FCSTD DOCUMENT  (FreeCAD 0.19R24276 (Git))
Label: Master_sketch
License: All rights reserved
LicenseURL: http://en.wikipedia.org/wiki/All_rights_reserved
objects: Sketcher::SketchObject×1, PartDesign::Body×1
note: 2 computed .brp shape members not serialized (recipe doc carries the construction recipe); baked Part::Feature solids carry a one-line shape summary decoded from their .brp

FEATURE [Sketcher::SketchObject] Sketch
  FullyConstrained = false
  MapMode = 5
  Support = -> [XY_Plane]
  sketch-geometry (44):
    g0: Circle CenterX=0 CenterY=-54 CenterZ=0 NormalX=0 NormalY=0 NormalZ=1 AngleXU=0 Radius=4
    g1: LineSegment StartX=-57.9645 StartY=-38.8963 StartZ=0 EndX=-1.26483 EndY=-57.7948 EndZ=0
    g2: LineSegment StartX=-45 StartY=0 StartZ=0 EndX=-57.9645 EndY=-38.8963 EndZ=0
    g3: LineSegment StartX=0 StartY=-54 StartZ=0 EndX=-1.26483 EndY=-57.7948 EndZ=0
    g4: LineSegment StartX=1.39757 StartY=-57.7479 StartZ=0 EndX=58.5823 EndY=-36.4241 EndZ=0
    g5: LineSegment StartX=45 StartY=0 StartZ=0 EndX=58.5823 EndY=-36.4241 EndZ=0
    g6: LineSegment StartX=0 StartY=-54 StartZ=0 EndX=1.39757 EndY=-57.7479 EndZ=0
    g7: LineSegment StartX=-45 StartY=0 StartZ=0 EndX=45 EndY=0 EndZ=0
    g8: LineSegment StartX=0 StartY=0 StartZ=0 EndX=0 EndY=-54 EndZ=0
    g9: Circle CenterX=0 CenterY=0 CenterZ=0 NormalX=0 NormalY=0 NormalZ=1 AngleXU=0 Radius=90
    g10: LineSegment StartX=-45 StartY=0 StartZ=0 EndX=-31.8819 EndY=-39.2255 EndZ=0
    g11: Circle CenterX=0 CenterY=54 CenterZ=0 NormalX=0 NormalY=0 NormalZ=1 AngleXU=0 Radius=4
    g12: LineSegment StartX=0 StartY=0 StartZ=0 EndX=0 EndY=54 EndZ=0
    g13: Circle CenterX=0 CenterY=220 CenterZ=0 NormalX=0 NormalY=0 NormalZ=1 AngleXU=0 Radius=20
    g14: LineSegment StartX=45 StartY=0 StartZ=0 EndX=56.689 EndY=42.3716 EndZ=0
    g15: LineSegment StartX=-29.7255 StartY=-48.3086 StartZ=0 EndX=-26.8797 EndY=-39.7704 EndZ=0
    g16: LineSegment StartX=-29.7255 StartY=-48.3086 StartZ=0 EndX=-32.5714 EndY=-56.8468 EndZ=0
    g17: Circle CenterX=-45 CenterY=0 CenterZ=0 NormalX=0 NormalY=0 NormalZ=1 AngleXU=0 Radius=41
    g18: Circle CenterX=45 CenterY=0 CenterZ=0 NormalX=0 NormalY=0 NormalZ=1 AngleXU=0 Radius=41
    g19: LineSegment StartX=-119.998 StartY=-134.375 StartZ=0 EndX=119.998 EndY=-135.625 EndZ=0
    g20: LineSegment StartX=0 StartY=0 StartZ=0 EndX=0 EndY=-135 EndZ=0
    g21: LineSegment StartX=-119.998 StartY=-134.375 StartZ=0 EndX=-94.9987 EndY=-134.505 EndZ=0
    g22: LineSegment StartX=-94.9987 StartY=-134.505 StartZ=0 EndX=-94.8737 EndY=-110.506 EndZ=0
    g23: LineSegment StartX=-94.8737 StartY=-110.506 StartZ=0 EndX=-119.873 EndY=-110.375 EndZ=0
    g24: LineSegment StartX=-119.873 StartY=-110.375 StartZ=0 EndX=-119.998 EndY=-134.375 EndZ=0
    g25: LineSegment StartX=119.998 StartY=-135.625 StartZ=0 EndX=94.9987 EndY=-135.495 EndZ=0
    g26: LineSegment StartX=94.9987 StartY=-135.495 StartZ=0 EndX=95.1237 EndY=-111.495 EndZ=0
    g27: LineSegment StartX=95.1237 StartY=-111.495 StartZ=0 EndX=120.123 EndY=-111.625 EndZ=0
    g28: LineSegment StartX=120.123 StartY=-111.625 StartZ=0 EndX=119.998 EndY=-135.625 EndZ=0
    g29: LineSegment StartX=0 StartY=-135 StartZ=0 EndX=-86.2867 EndY=-103.084 EndZ=0
    g30: LineSegment StartX=0 StartY=-135 StartZ=0 EndX=86.6144 EndY=-103.985 EndZ=0
    g31: LineSegment StartX=86.6144 StartY=-103.985 StartZ=0 EndX=97.6158 EndY=-134.708 EndZ=0
    g32: LineSegment StartX=97.6158 StartY=-134.708 StartZ=0 EndX=128.339 EndY=-123.706 EndZ=0
    g33: LineSegment StartX=128.339 StartY=-123.706 StartZ=0 EndX=117.337 EndY=-92.9833 EndZ=0
    g34: LineSegment StartX=-86.2867 StartY=-103.084 StartZ=0 EndX=-110.929 EndY=-107.297 EndZ=0
    g35: LineSegment StartX=-110.929 StartY=-107.297 StartZ=0 EndX=-115.142 EndY=-82.6549 EndZ=0
    g36: LineSegment StartX=-115.142 StartY=-82.6549 StartZ=0 EndX=-90.4997 EndY=-78.442 EndZ=0
    g37: LineSegment StartX=-90.4997 StartY=-78.442 StartZ=0 EndX=-86.2867 EndY=-103.084 EndZ=0
    g38: LineSegment StartX=-100.714 StartY=-92.8697 StartZ=0 EndX=-90.4997 EndY=-78.442 EndZ=0
    g39: LineSegment StartX=-115.142 StartY=-82.6549 StartZ=0 EndX=-86.2867 EndY=-103.084 EndZ=0
    g40: LineSegment StartX=-31.8812 StartY=-137.215 StartZ=0 EndX=34.0407 EndY=-137.215 EndZ=0
    g41: LineSegment StartX=34.0407 StartY=-137.215 StartZ=0 EndX=34.0407 EndY=-145.036 EndZ=0
    g42: LineSegment StartX=34.0407 StartY=-145.036 StartZ=0 EndX=-31.8812 EndY=-145.036 EndZ=0
    g43: LineSegment StartX=-31.8812 StartY=-145.036 StartZ=0 EndX=-31.8812 EndY=-137.215 EndZ=0
  constraints (109):
    c: Diameter(g0) = 8
    c: PointOnObject(g1,g0)
    c: Perpendicular(g1,g2)
    c: Coincident(g3,g0)
    c: Coincident(g3,g1)
    c: Perpendicular(g3,g1)
    c: PointOnObject(g4,g0)
    c: Coincident(g5,g4)
    c: Perpendicular(g5,g4)
    c: Coincident(g6,g0)
    c: Coincident(g6,g4)
    c: Perpendicular(g4,g6)
    c: Distance(g7) = 90
    c: Coincident(g8,g-1)
    c: Coincident(g8,g0)
    c: Perpendicular(g7,g8)
    c: Distance(g8) = 54
    c: Coincident(g9,g-1)
    c: Diameter(g9) = 180
    c: Equal(g0,g11)
    c: Coincident(g12,g-1)
    c: Coincident(g12,g11)
    c: Equal(g12,g8)
    c: Parallel(g12,g8)
    c: PointOnObject(g13,g-2)
    c: Radius(g13) = 20
    c: DistanceY(g-1,g13) = 220
    c: PointOnObject(g15,g1)
    c: Coincident(g16,g15)
    c: Symmetric(g16,g15,g15)
    c: Distance(g16,g15) = 18
    c: Perpendicular(g15,g1)
    c: Distance(g15,g1) = 30
    c: Coincident(g17,g2)
    c: Coincident(g18,g5)
    c: Equal(g17,g18)
    c: Coincident(g20,g-1)
    c: Vertical(g20)
    c: DistanceY(g20,g20) = 135
    c: Symmetric(g19,g19,g20)
    c: Distance(g19) = 240
    c: Coincident(g21,g22)
    c: Coincident(g22,g23)
    c: Coincident(g23,g24)
    c: Coincident(g24,g21)
    c: Coincident(g21,g19)
    c: Parallel(g22,g24)
    c: Equal(g24,g22)
    c: Parallel(g21,g19)
    c: Perpendicular(g19,g22)
    c: Coincident(g25,g26)
    c: Coincident(g26,g27)
    c: Coincident(g27,g28)
    c: Coincident(g28,g25)
    c: Parallel(g26,g28)
    c: Equal(g28,g26)
    c: Coincident(g25,g19)
    c: Parallel(g25,g19)
    c: Perpendicular(g19,g26)
    c: Equal(g24,g26)
    c: Distance(g19,g21) = 25
    c: Distance(g25,g19) = 25
    c: Distance(g23,g19) = 24
    c: Angle(g29,g19) = 0.349066
    c: Angle(g19,g30) = 0.349066
    c: Coincident(g29,g30)
    c: Coincident(g29,g20)
    c: Distance(g29) = 92
    c: Equal(g29,g30)
    c: Coincident(g31,g30)
    c: Coincident(g32,g31)
    c: Coincident(g33,g32)
    c: PointOnObject(g33,g30)
    c: Parallel(g33,g31)
    c: Perpendicular(g30,g31)
    c: Parallel(g32,g30)
    c: Equal(g31,g32)
    c: Coincident(g34,g29)
    c: Coincident(g35,g34)
    c: Coincident(g36,g35)
    c: Coincident(g37,g36)
    c: Coincident(g37,g29)
    c: Parallel(g35,g37)
    c: Perpendicular(g35,g34)
    c: Equal(g35,g36)
    c: Distance(g34) = 25
    c: Coincident(g38,g36)
    c: Coincident(g39,g35)
    c: Coincident(g39,g29)
    c: Symmetric(g35,g29,g38)
    c: Coincident(g2,g7)
    c: Coincident(g10,g2)
    c: Coincident(g7,g5)
    c: Coincident(g7,g14)
    c: Symmetric(g2,g5,g-1)
    c: Horizontal(g7)
    c: PointOnObject(g2,g17)
    c: Coincident(g1,g2)
    c: Diameter(g17) = 82
    c: Parallel(g34,g36)
    c: Angle(g34,g29) = 2.61799
    c: Coincident(g40,g41)
    c: Coincident(g41,g42)
    c: Coincident(g42,g43)
    c: Coincident(g43,g40)
    c: Horizontal(g40)
    c: Horizontal(g42)
    c: Vertical(g41)
    c: Vertical(g43)
FEATURE [PartDesign::Body] Body
  Group = -> [Sketch]
  Origin = -> Origin
